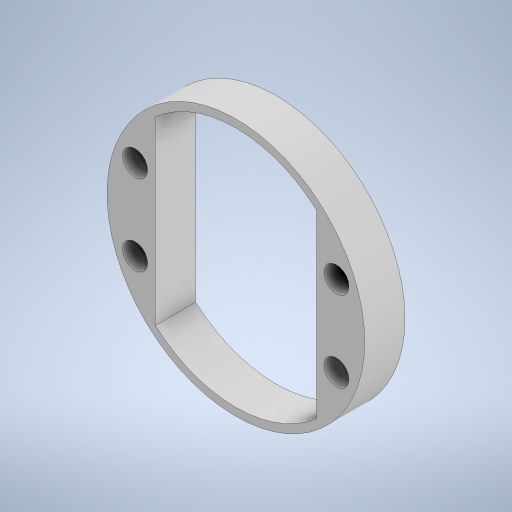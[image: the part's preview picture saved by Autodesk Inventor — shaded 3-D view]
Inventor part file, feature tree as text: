
AUTODESK INVENTOR PART (.ipt)
format: ipt  version: 2023.4 (Build 274418000, 418)  size: 258,560 bytes
history: native  units: mm
features: extrude x2, sketch x2
ambient origin geometry x8: Origin, YZ Plane, XZ Plane, XY Plane, X Axis, Y Axis, Z Axis, Center Point
bodies: Solid1 (feature_tree)
feature tree (4):
  extrude  "Extrusion1"  TaperAngle=0.0deg  [1 undecoded]
  extrude  "Extrusion2"  [1 undecoded]
  sketch  "Sketch1"  dims[d2=5.0mm d3=0.0mm d7=0.0mm d8=0.0mm]
  sketch  "Sketch2"
note: 2 required parameter values undecoded (feature->parameter linkage not recoverable at this tier; creation-order binding heuristic only, values carry confidence <= 0.55)
